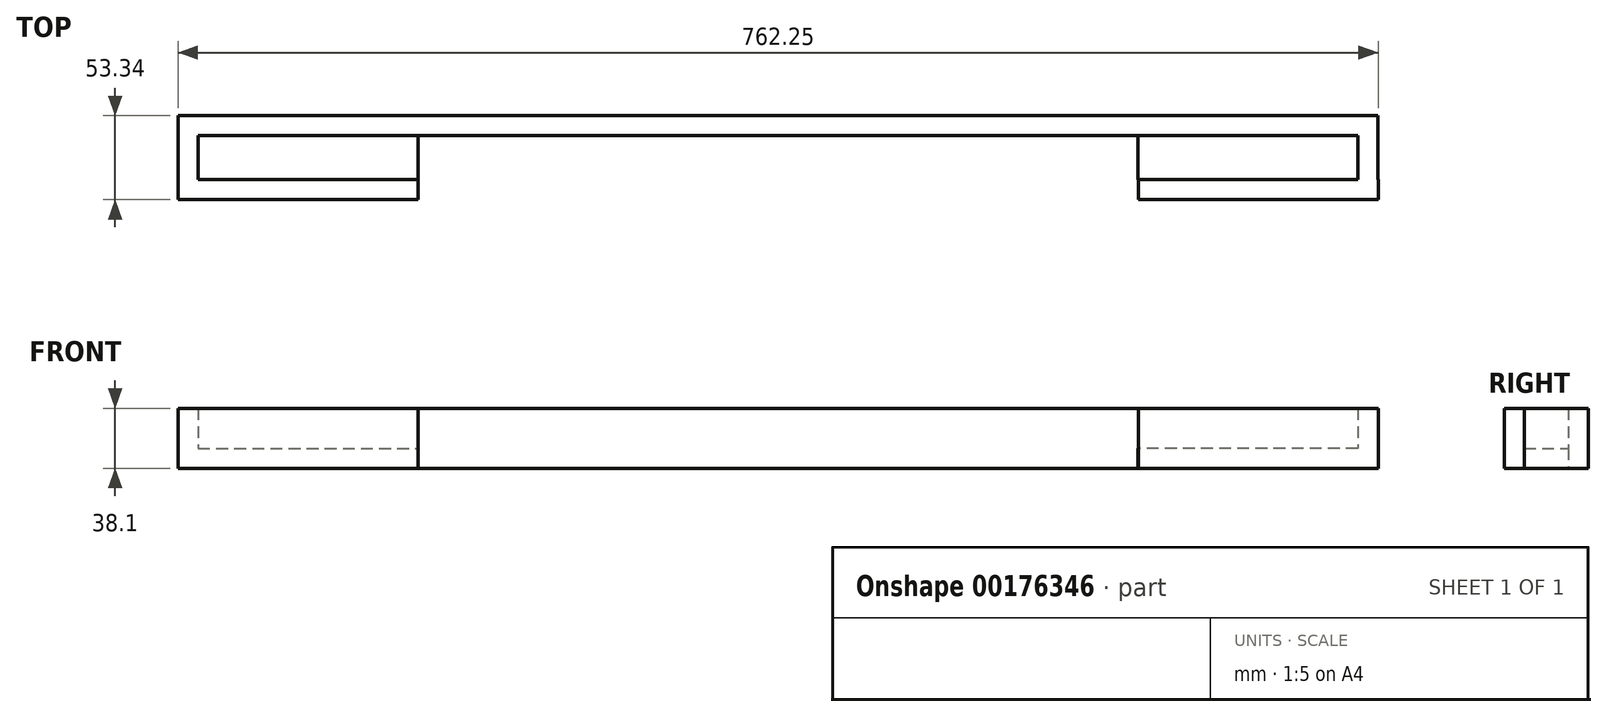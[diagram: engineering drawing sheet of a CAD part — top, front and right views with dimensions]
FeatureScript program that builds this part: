
annotation { "Feature Type Name" : "Feature", "Feature Type Description" : "" }
export const myFeature = defineFeature(function(context is Context, id is Id, definition is map)
    precondition{}
    {
        {
            var Q0;
            Q0=qCreatedBy(makeId("Front.planeOp"),FACE);
            var sketch = newSketch(context, id + "F0", { "sketchPlane" : qUnion([Q0])});
            skLineSegment(sketch, "E0.bottom", {"start": v(-381, 19.05) * mm, "end": v(381, 19.05) * mm});
            skLineSegment(sketch, "E0.top", {"start": v(-381, -19.05) * mm, "end": v(381, -19.05) * mm});
            skLineSegment(sketch, "E0.left", {"start": v(-381, 19.05) * mm, "end": v(-381, -19.05) * mm});
            skLineSegment(sketch, "E0.right", {"start": v(381, 19.05) * mm, "end": v(381, -19.05) * mm});
            skPoint(sketch, "E0.middle", {"position": v(0, 0) * mm});
            skLineSegment(sketch, "E1", {"start": v(-368.3, 19.05) * mm, "end": v(-368.3, -6.35) * mm});
            skLineSegment(sketch, "E2", {"start": v(-368.3, -6.35) * mm, "end": v(-228.6, -6.35) * mm});
            skLineSegment(sketch, "E3", {"start": v(-228.6, -6.35) * mm, "end": v(-228.6, -19.05) * mm});
            skLineSegment(sketch, "E4", {"start": v(368.3, 19.05) * mm, "end": v(368.3, -6.35) * mm});
            skLineSegment(sketch, "E5", {"start": v(368.3, -6.35) * mm, "end": v(228.6, -6.35) * mm});
            skLineSegment(sketch, "E6", {"start": v(228.6, -6.35) * mm, "end": v(228.6, -19.05) * mm});
            skSolve(sketch);
        }
        {
            var Q0;
            {var subQ0=sQuery(id+"F0.wireOp",EDGE,"E1");Q0=makeQuery(id+"F0.imprint","IMPRINT",FACE,{"disambiguationData":[TD([[makeQuery(id+"F0.imprint","IMPRINT",EDGE,{"derivedFrom":subQ0}),1.0]])]});}
            var Q1;
            {var subQ1=sQuery(id+"F0.wireOp",EDGE,"E0.left");Q1=makeQuery(id+"F0.imprint","IMPRINT",FACE,{"disambiguationData":[TD([[makeQuery(id+"F0.imprint","IMPRINT",EDGE,{"derivedFrom":subQ1}),1.0]])]});}
            var Q2;
            {var subQ1=sQuery(id+"F0.wireOp",EDGE,"E0.right");Q2=makeQuery(id+"F0.imprint","IMPRINT",FACE,{"disambiguationData":[TD([[makeQuery(id+"F0.imprint","IMPRINT",EDGE,{"derivedFrom":subQ1}),-1.0]])]});}
            extrude(context, id + "F1", {"entities" : qUnion([Q0, Q1, Q2]), "oppositeDirection" : true, "depth" : 12.7 * mm});
        }
        {
            var Q0;
            {var subQ1=sQuery(id+"F0.wireOp",EDGE,"E0.left");Q0=makeQuery(id+"F0.imprint","IMPRINT",FACE,{"disambiguationData":[TD([[makeQuery(id+"F0.imprint","IMPRINT",EDGE,{"derivedFrom":subQ1}),1.0]])]});}
            var Q1;
            {var subQ1=sQuery(id+"F0.wireOp",EDGE,"E0.right");Q1=makeQuery(id+"F0.imprint","IMPRINT",FACE,{"disambiguationData":[TD([[makeQuery(id+"F0.imprint","IMPRINT",EDGE,{"derivedFrom":subQ1}),-1.0]])]});}
            extrude(context, id + "F2", {"entities" : qUnion([Q0, Q1]), "operationType" : NewBodyOperationType.ADD, "depth" : 27.94 * mm});
        }
        {
            var Q0;
            Q0=makeQuery(id+"F2.opExtrude","CAP_FACE",FACE,{"disambiguationData":[OSD([sQuery(id+"F0.wireOp",EDGE,"E0.bottom"),sQuery(id+"F0.wireOp",EDGE,"E0.top"),sQuery(id+"F0.wireOp",EDGE,"E0.left"),sQuery(id+"F0.wireOp",EDGE,"E1"),sQuery(id+"F0.wireOp",EDGE,"E2"),sQuery(id+"F0.wireOp",EDGE,"E3")])],"isStart":false});
            var sketch = newSketch(context, id + "F3", { "sketchPlane" : qUnion([Q0])});
            skLineSegment(sketch, "E7.bottom", {"start": v(-381, 19.05) * mm, "end": v(-228.6, 19.05) * mm});
            skLineSegment(sketch, "E7.top", {"start": v(-381, -19.05) * mm, "end": v(-228.6, -19.05) * mm});
            skLineSegment(sketch, "E7.left", {"start": v(-381, 19.05) * mm, "end": v(-381, -19.05) * mm});
            skLineSegment(sketch, "E7.right", {"start": v(-228.6, 19.05) * mm, "end": v(-228.6, -19.05) * mm});
            skLineSegment(sketch, "E8.bottom", {"start": v(381.25, -19.05) * mm, "end": v(228.86, -19.05) * mm});
            skLineSegment(sketch, "E8.top", {"start": v(381.25, 19.05) * mm, "end": v(228.86, 19.05) * mm});
            skLineSegment(sketch, "E8.left", {"start": v(381.25, -19.05) * mm, "end": v(381.25, 19.05) * mm});
            skLineSegment(sketch, "E8.right", {"start": v(228.86, -19.05) * mm, "end": v(228.86, 19.05) * mm});
            skSolve(sketch);
        }
        {
            var Q0;
            {var subQ1=makeQuery(id+"F2.opExtrude","CAP_EDGE",EDGE,{"disambiguationData":[OSD([sQuery(id+"F0.wireOp",EDGE,"E1")])],"isStart":false});Q0=makeQuery(id+"F3.imprint","IMPRINT",FACE,{"disambiguationData":[TD([[makeQuery(id+"F3.imprint","IMPRINT",EDGE,{"derivedFrom":subQ1}),1.0]])]});}
            var Q1;
            {var subQ2=sQuery(id+"F3.wireOp",EDGE,"E7.top");Q1=makeQuery(id+"F3.imprint","IMPRINT",FACE,{"disambiguationData":[TD([[makeQuery(id+"F3.imprint","IMPRINT",EDGE,{"derivedFrom":subQ2}),1.0]])]});}
            var Q2;
            Q2=makeQuery(id+"F3.imprint","IMPRINT",FACE,{"disambiguationData":[TD([[makeQuery(id+"F3.imprint","IMPRINT",EDGE,{"derivedFrom":sQuery(id+"F3.wireOp",EDGE,"E8.bottom")}),-1.0]])]});
            extrude(context, id + "F4", {"entities" : qUnion([Q0, Q1, Q2]), "operationType" : NewBodyOperationType.ADD, "depth" : 12.7 * mm});
        }
    });
